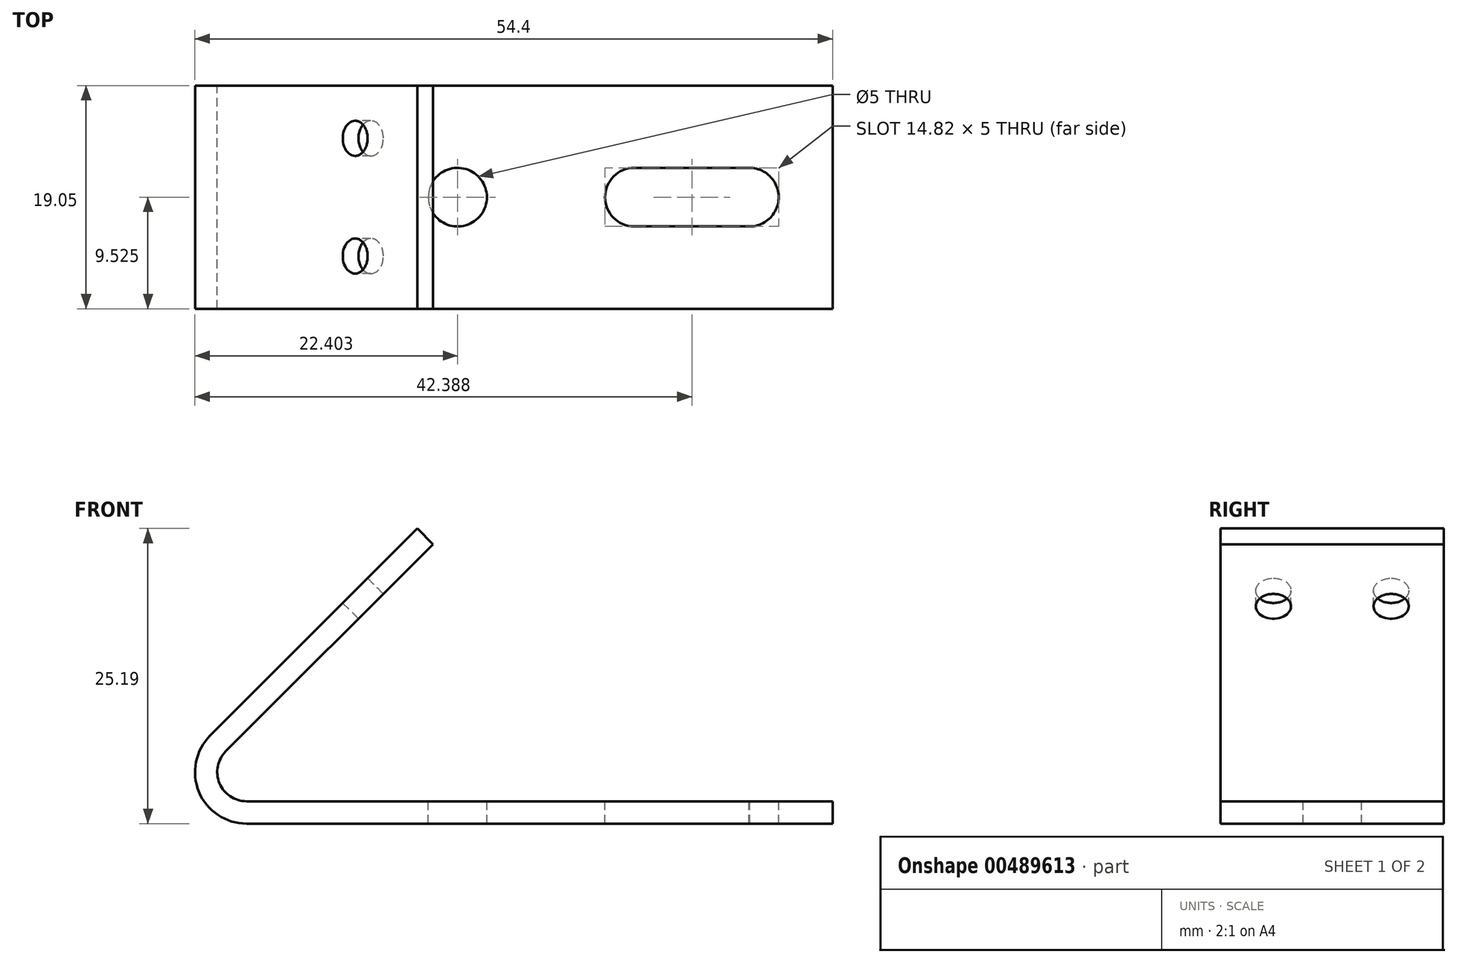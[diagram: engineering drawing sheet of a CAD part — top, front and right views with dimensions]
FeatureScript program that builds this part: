
annotation { "Feature Type Name" : "Feature", "Feature Type Description" : "" }
export const myFeature = defineFeature(function(context is Context, id is Id, definition is map)
    precondition{}
    {
        {
            var Q0;
            Q0=qCreatedBy(makeId("Front.planeOp"),FACE);
            var sketch = newSketch(context, id + "F0", { "sketchPlane" : qUnion([Q0])});
            skLineSegment(sketch, "E0", {"start": v(31.25, 0) * mm, "end": v(-18.75, 0) * mm});
            skLineSegment(sketch, "E1", {"start": v(-21.86, 7.51) * mm, "end": v(-4.18, 25.19) * mm});
            skLineSegment(sketch, "E2", {"start": v(-4.18, 25.19) * mm, "end": v(-2.84, 23.85) * mm});
            skLineSegment(sketch, "E3", {"start": v(31.25, 0) * mm, "end": v(31.25, 1.9) * mm});
            skLineSegment(sketch, "E4", {"start": v(31.25, 1.9) * mm, "end": v(-18.75, 1.9) * mm});
            skLineSegment(sketch, "E5", {"start": v(-20.51, 6.17) * mm, "end": v(-2.84, 23.85) * mm});
            skPoint(sketch, "E6.visualSharp", {"position": v(-29.37, 0) * mm});
            skArc(sketch, "E6.filletArc", {"start": v(-21.86, 7.51) * mm, "mid": v(-22.81, 2.72) * mm, "end": v(-18.75, 0) * mm});
            skPoint(sketch, "E7.visualSharp", {"position": v(-24.78, 1.9) * mm});
            skArc(sketch, "E8", {"start": v(-20.51, 6.17) * mm, "mid": v(-21.06, 3.44) * mm, "end": v(-18.75, 1.9) * mm});
            skSolve(sketch);
        }
        {
            var Q0;
            Q0 = qSketchRegion(id + "F0", true);
            extrude(context, id + "F1", {"entities" : qUnion([Q0]), "depth" : 19.05 * mm});
        }
        {
            var Q0;
            Q0=makeQuery(id+"F1.opExtrude","SWEPT_FACE",FACE,{"disambiguationData":[OSD([sQuery(id+"F0.wireOp",EDGE,"E4")])]});
            var sketch = newSketch(context, id + "F2", { "sketchPlane" : qUnion([Q0])});
            skLineSegment(sketch, "E9", {"start": v(31.25, -9.53) * mm, "end": v(-0.75, -9.53) * mm, "construction": true});
            skCircle(sketch, "E10", {"center": v(-0.75, -9.53) * mm, "radius": 2.5 * mm});
            skLineSegment(sketch, "E11", {"start": v(31.25, -9.53) * mm, "end": v(31.25, -7.03) * mm, "construction": true});
            skLineSegment(sketch, "E12", {"start": v(31.25, -7.03) * mm, "end": v(26.75, -7.03) * mm, "construction": true});
            skLineSegment(sketch, "E13.bottom", {"start": v(24.19, -7.03) * mm, "end": v(14.33, -7.03) * mm});
            skLineSegment(sketch, "E13.top", {"start": v(24.19, -12.03) * mm, "end": v(14.33, -12.03) * mm});
            skArc(sketch, "E14", {"start": v(14.33, -7.03) * mm, "mid": v(11.83, -9.53) * mm, "end": v(14.33, -12.03) * mm});
            skArc(sketch, "E15", {"start": v(24.1, -7.03) * mm, "mid": v(26.65, -9.49) * mm, "end": v(24.19, -12.03) * mm});
            skSolve(sketch);
        }
        {
            var Q0;
            Q0 = qSketchRegion(id + "F2", true);
            extrude(context, id + "F3", {"entities" : qUnion([Q0]), "operationType" : NewBodyOperationType.REMOVE, "endBound" : BoundingType.UP_TO_NEXT, "oppositeDirection" : true, "depth" : 25 * mm});
        }
        {
            var Q0;
            Q0=makeQuery(id+"F1.opExtrude","SWEPT_FACE",FACE,{"disambiguationData":[OSD([sQuery(id+"F0.wireOp",EDGE,"E1")])]});
            var sketch = newSketch(context, id + "F4", { "sketchPlane" : qUnion([Q0])});
            skLineSegment(sketch, "E16", {"start": v(19.05, 7.36) * mm, "end": v(14.55, 7.36) * mm, "construction": true});
            skLineSegment(sketch, "E17", {"start": v(14.55, 7.36) * mm, "end": v(14.55, 14.86) * mm, "construction": true});
            skCircle(sketch, "E18", {"center": v(14.55, 7.36) * mm, "radius": 1.5 * mm});
            skLineSegment(sketch, "E19", {"start": v(0, 7.36) * mm, "end": v(4.5, 7.36) * mm, "construction": true});
            skCircle(sketch, "E20", {"center": v(4.5, 7.36) * mm, "radius": 1.5 * mm});
            skSolve(sketch);
        }
        {
            var Q0;
            Q0 = qSketchRegion(id + "F4", true);
            extrude(context, id + "F5", {"entities" : qUnion([Q0]), "operationType" : NewBodyOperationType.REMOVE, "endBound" : BoundingType.UP_TO_NEXT, "oppositeDirection" : true, "depth" : 25.4 * mm});
        }
    });
